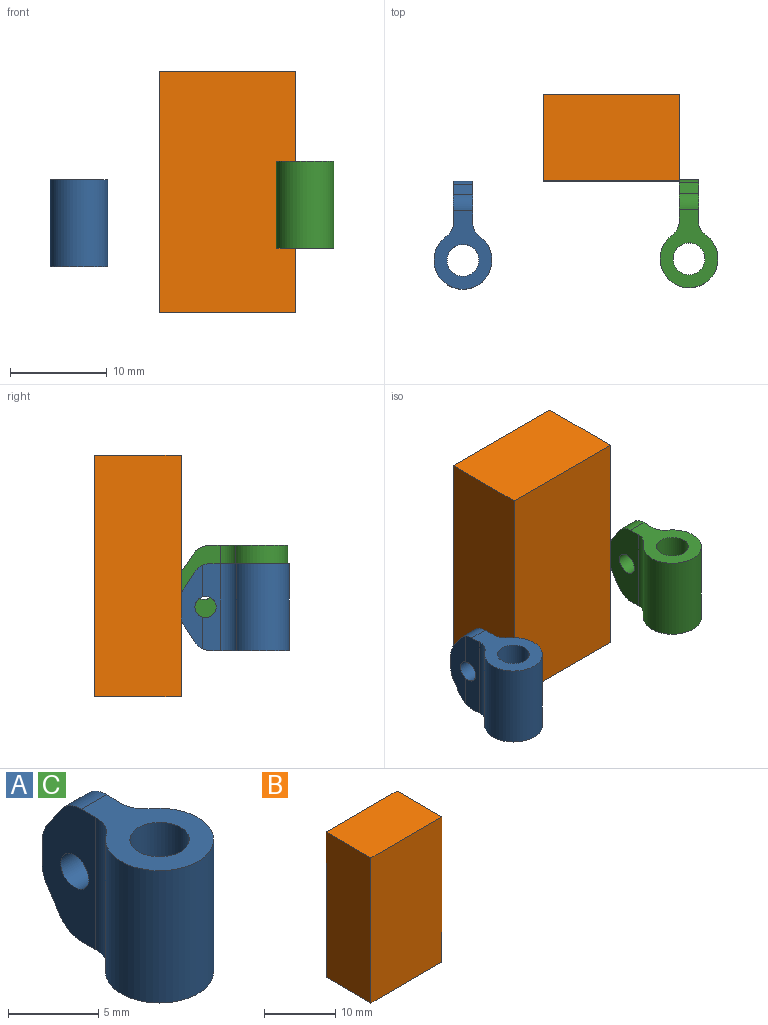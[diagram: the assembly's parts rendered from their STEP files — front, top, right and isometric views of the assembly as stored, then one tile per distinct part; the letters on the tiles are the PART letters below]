
ASSEMBLY  parts=3 mates=1
PART A: 17 faces, bbox 6x11.2x9 mm
  f0: plane 2x1.79mm, normal (0,1,0), area 3.6mm2, adj f1,f4,f12,f13
  f1: plane 9x4.2mm, normal (-1,0,0), area 27.6mm2, adj f0,f6,f7,f8,f9,f10,f11,f12
  f2: cylinder r=3mm len=9mm, axis (0,0,-1), area 135.3mm2, adj f6,f7,f15,f16
  f3: plane 9x1.91mm, normal (1,-0.03,0), area 14.4mm2, adj f4,f6,f7,f8,f11,f14,f15
  f4: plane 8.6x2.2mm, normal (1,0,0), area 12.3mm2, adj f0,f3,f8,f9,f10,f11,f12,f13
  f5: cylinder r=1.65mm len=9mm, axis (0,0,-1), area 93.3mm2, adj f6,f7
  f6: plane 8.13x6mm, normal (0,0,1), area 24.4mm2, adj f1,f2,f3,f5,f11,f15,f16
  f7: plane 8.13x6mm, normal (0,0,-1), area 24.4mm2, adj f1,f2,f3,f5,f14,f15,f16
  f8: cylinder r=1.1mm len=2.2mm, axis (1,0,0), area 13.7mm2, adj f1,f3,f4
  f9: plane 2x1.61mm, normal (0,0.83,-0.55), area 3.9mm2, adj f1,f4,f12,f14
  f10: plane 2x1.61mm, normal (0,0.83,0.55), area 3.9mm2, adj f1,f4,f11,f13
  f11: cylinder r=2mm len=2mm, axis (1,0,0), area 3.9mm2, adj f1,f3,f4,f6,f10
  f12: cylinder r=2mm len=2mm, axis (-1,0,0), area 2.4mm2, adj f0,f1,f4,f9
  f13: cylinder r=2mm len=2mm, axis (-1,0,0), area 2.4mm2, adj f0,f1,f4,f10
  f14: cylinder r=2mm len=2mm, axis (-1,0,0), area 3.9mm2, adj f1,f3,f4,f7,f9
  f15: cylinder r=2mm len=9mm, axis (0,0,-1), area 17.4mm2, adj f2,f3,f6,f7
  f16: cylinder r=2mm len=9mm, axis (0,0,-1), area 16.7mm2, adj f1,f2,f6,f7
PART B: 6 faces, bbox 14.1x8.9x25 mm
  f0: plane 25x14.12mm, normal (0,-1,0), area 353mm2, adj f1,f3,f4,f5
  f1: plane 25x8.93mm, normal (1,0,0), area 223.3mm2, adj f0,f2,f4,f5
  f2: plane 25x14.12mm, normal (0,1,0), area 353mm2, adj f1,f3,f4,f5
  f3: plane 25x8.93mm, normal (-1,0,0), area 223.3mm2, adj f0,f2,f4,f5
  f4: plane 14.12x8.93mm, normal (0,0,1), area 126.1mm2, adj f0,f1,f2,f3
  f5: plane 14.12x8.93mm, normal (0,0,-1), area 126.1mm2, adj f0,f1,f2,f3
PART C: same geometry as A
PLACE A rot(axis=(0,-1,0),180deg) t=(-15.36,-12.67,13.78)mm
PLACE B at identity
PLACE C t=(8.06,-12.53,6.66)mm
MATE planar C.f1 <-> B.f1  axis (-1,0,0) through (7.06,-7.96,15.66)mm
